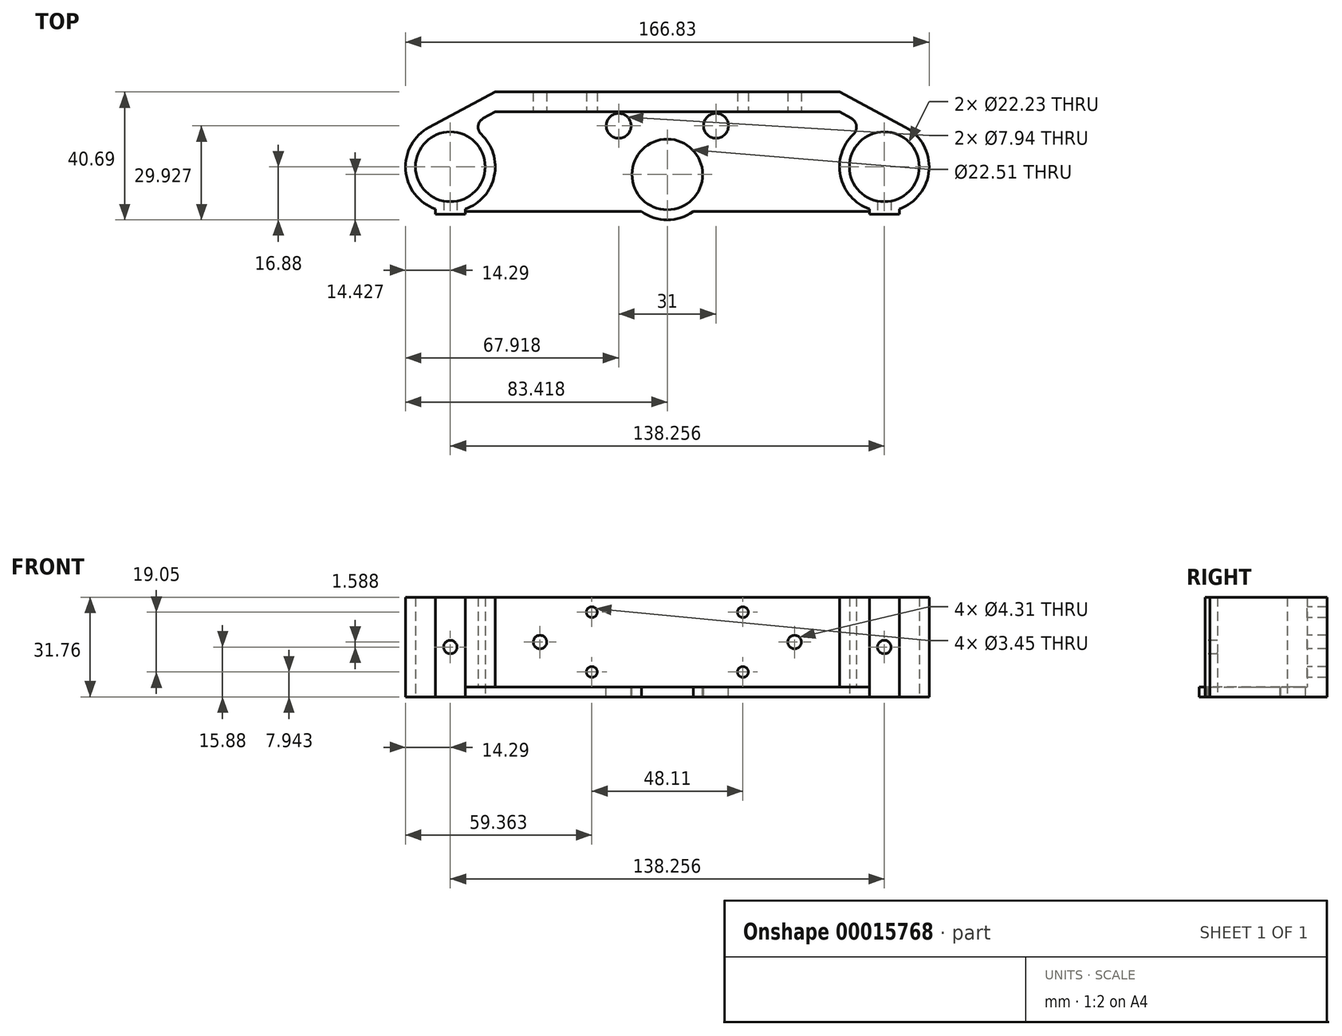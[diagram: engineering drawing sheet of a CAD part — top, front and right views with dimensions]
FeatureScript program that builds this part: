
annotation { "Feature Type Name" : "Feature", "Feature Type Description" : "" }
export const myFeature = defineFeature(function(context is Context, id is Id, definition is map)
    precondition{}
    {
        {
            var Q0;
            Q0=qCreatedBy(makeId("Top.planeOp"),FACE);
            var sketch = newSketch(context, id + "F0", { "sketchPlane" : qUnion([Q0])});
            skCircle(sketch, "E0", {"center": v(0, 0) * mm, "radius": 11.11 * mm});
            skLineSegment(sketch, "E1.bottom", {"start": v(14.29, 17.46) * mm, "end": v(123.97, 17.46) * mm});
            skLineSegment(sketch, "E2", {"start": v(69.13, 17.46) * mm, "end": v(69.13, 23.81) * mm, "construction": true});
            skCircle(sketch, "E3", {"center": v(138.26, 0) * mm, "radius": 11.11 * mm});
            skLineSegment(sketch, "E4", {"start": v(14.29, 23.81) * mm, "end": v(123.97, 23.81) * mm});
            skLineSegment(sketch, "E5", {"start": v(-6.72, 12.6) * mm, "end": v(14.29, 23.81) * mm});
            skLineSegment(sketch, "E6", {"start": v(123.97, 23.81) * mm, "end": v(144.98, 12.6) * mm});
            skLineSegment(sketch, "E7", {"start": v(0, 0) * mm, "end": v(138.26, 0) * mm, "construction": true});
            skLineSegment(sketch, "E8", {"start": v(69.13, 17.46) * mm, "end": v(69.13, 0) * mm, "construction": true});
            skLineSegment(sketch, "E9", {"start": v(123.97, 17.46) * mm, "end": v(132.33, 13) * mm});
            skLineSegment(sketch, "E10", {"start": v(128.15, 15.23) * mm, "end": v(130.79, 20.18) * mm, "construction": true});
            skLineSegment(sketch, "E11", {"start": v(5.92, 13) * mm, "end": v(14.29, 17.46) * mm});
            skArc(sketch, "E12", {"start": v(4.76, -13.47) * mm, "mid": v(14.27, -0.63) * mm, "end": v(5.92, 13) * mm});
            skArc(sketch, "E13", {"start": v(-6.72, 12.6) * mm, "mid": v(-14.25, -1.07) * mm, "end": v(-4.76, -13.47) * mm});
            skLineSegment(sketch, "E14", {"start": v(0, 0) * mm, "end": v(0, -13.47) * mm, "construction": true});
            skLineSegment(sketch, "E15", {"start": v(138.26, 0) * mm, "end": v(138.26, -13.47) * mm, "construction": true});
            skLineSegment(sketch, "E16.bottom", {"start": v(-4.76, -13.47) * mm, "end": v(4.76, -13.47) * mm, "construction": true});
            skLineSegment(sketch, "E16.top", {"start": v(-4.76, -15.06) * mm, "end": v(4.76, -15.06) * mm});
            skLineSegment(sketch, "E16.left", {"start": v(-4.76, -13.47) * mm, "end": v(-4.76, -15.06) * mm});
            skLineSegment(sketch, "E16.right", {"start": v(4.76, -13.47) * mm, "end": v(4.76, -15.06) * mm});
            skLineSegment(sketch, "E17.bottom", {"start": v(133.5, -13.47) * mm, "end": v(143.02, -13.47) * mm, "construction": true});
            skLineSegment(sketch, "E17.top", {"start": v(133.5, -15.06) * mm, "end": v(143.02, -15.06) * mm});
            skLineSegment(sketch, "E17.left", {"start": v(133.5, -13.47) * mm, "end": v(133.5, -15.06) * mm});
            skLineSegment(sketch, "E17.right", {"start": v(143.02, -13.47) * mm, "end": v(143.02, -15.06) * mm});
            skArc(sketch, "E18", {"start": v(132.33, 13) * mm, "mid": v(123.98, -0.63) * mm, "end": v(133.5, -13.47) * mm});
            skArc(sketch, "E19", {"start": v(143.02, -13.47) * mm, "mid": v(152.5, -1.07) * mm, "end": v(144.98, 12.6) * mm});
            skSolve(sketch);
        }
        {
            var Q0;
            Q0=qSketchRegion(id+"F0",true);
            extrude(context, id + "F1", {"entities" : qUnion([Q0]), "depth" : 28.57 * mm});
        }
        {
            var Q0;
            Q0=makeQuery(id+"F1.opExtrude","CAP_FACE",FACE,{"disambiguationData":[OSD([sQuery(id+"F0.wireOp",EDGE,"E0"),sQuery(id+"F0.wireOp",EDGE,"2iOkBpD2-QLiU-HpJU-IKXQ-EcRK06cCBt2a"),sQuery(id+"F0.wireOp",EDGE,"E1.bottom"),sQuery(id+"F0.wireOp",EDGE,"LR8YGM2p-kzYz-Rjs2-wGc3-v6aphVCy7C40"),sQuery(id+"F0.wireOp",EDGE,"E3"),sQuery(id+"F0.wireOp",EDGE,"E4"),sQuery(id+"F0.wireOp",EDGE,"E5"),sQuery(id+"F0.wireOp",EDGE,"E6"),sQuery(id+"F0.wireOp",EDGE,"E9"),sQuery(id+"F0.wireOp",EDGE,"E11")])],"isStart":true});
            var sketch = newSketch(context, id + "F2", { "sketchPlane" : qUnion([Q0])});
            skLineSegment(sketch, "E20", {"start": v(0, 0) * mm, "end": v(0, 14.29) * mm, "construction": true});
            skLineSegment(sketch, "E21", {"start": v(138.26, 14.29) * mm, "end": v(138.26, 0) * mm, "construction": true});
            skLineSegment(sketch, "E22", {"start": v(138.26, 0) * mm, "end": v(0, 0) * mm, "construction": true});
            skLineSegment(sketch, "E23", {"start": v(69.13, 0) * mm, "end": v(69.13, 2.45) * mm, "construction": true});
            skCircle(sketch, "E24", {"center": v(69.13, 2.45) * mm, "radius": 11.25 * mm});
            skLineSegment(sketch, "E25", {"start": v(138.26, 14.29) * mm, "end": v(77.38, 14.29) * mm});
            skLineSegment(sketch, "E26", {"start": v(0, 14.29) * mm, "end": v(60.87, 14.29) * mm});
            skArc(sketch, "E27", {"start": v(77.38, 14.29) * mm, "mid": v(69.13, 16.88) * mm, "end": v(60.87, 14.29) * mm});
            skLineSegment(sketch, "E28", {"start": v(69.13, 0) * mm, "end": v(69.13, -13.05) * mm, "construction": true});
            skLineSegment(sketch, "E29", {"start": v(84.63, -13.05) * mm, "end": v(53.63, -13.05) * mm, "construction": true});
            skCircle(sketch, "E30", {"center": v(84.63, -13.05) * mm, "radius": 3.97 * mm});
            skCircle(sketch, "E31", {"center": v(53.63, -13.05) * mm, "radius": 3.97 * mm});
            skSolve(sketch);
        }
        {
            var Q0;
            Q0=makeQuery(id+"F2.imprint","IMPRINT",FACE,{"disambiguationData":[TD([[makeQuery(id+"F2.imprint","IMPRINT",EDGE,{"derivedFrom":makeQuery(id+"F1.opExtrude","CAP_EDGE",EDGE,{"disambiguationData":[OSD([sQuery(id+"F0.wireOp",EDGE,"E0")])],"isStart":true})}),1.0]])]});
            var Q1;
            {var subQ2=sQuery(id+"F2.wireOp",EDGE,"SS8bNy7h-Ow7b-Kn8b-ZiMt-BjL3enOZ3Box");Q1=makeQuery(id+"F2.imprint","IMPRINT",FACE,{"disambiguationData":[TD([[makeQuery(id+"F2.imprint","IMPRINT",EDGE,{"derivedFrom":subQ2}),-1.0]])]});}
            var Q2;
            Q2=makeQuery(id+"F2.imprint","IMPRINT",FACE,{"disambiguationData":[TD([[makeQuery(id+"F2.imprint","IMPRINT",EDGE,{"derivedFrom":sQuery(id+"F2.wireOp",EDGE,"E24")}),-1.0]])]});
            extrude(context, id + "F3", {"entities" : qUnion([Q0, Q1, Q2]), "operationType" : NewBodyOperationType.ADD, "depth" : 3.17 * mm});
        }
        {
            var Q0;
            Q0=makeQuery(id+"F1.opExtrude","SWEPT_EDGE",EDGE,{"disambiguationData":[OSD([sQuery(id+"F0.wireOp",EDGE,"E11"),sQuery(id+"F0.wireOp",EDGE,"E12")])]});
            var Q1;
            Q1=makeQuery(id+"F1.opExtrude","SWEPT_EDGE",EDGE,{"disambiguationData":[OSD([sQuery(id+"F0.wireOp",EDGE,"E9"),sQuery(id+"F0.wireOp",EDGE,"E18")])]});
            fillet(context, id + "F4", {"entities" : qUnion([Q0, Q1]), "radius" : 3.17 * mm, "tangentPropagation" : true, "allowEdgeOverflow" : false});
        }
        {
            var Q0;
            Q0=makeQuery(id+"F1.opExtrude","SWEPT_FACE",FACE,{"disambiguationData":[OSD([sQuery(id+"F0.wireOp",EDGE,"E1.bottom")])]});
            var sketch = newSketch(context, id + "F5", { "sketchPlane" : qUnion([Q0])});
            skLineSegment(sketch, "E32", {"start": v(14.29, 14.29) * mm, "end": v(28.57, 14.29) * mm, "construction": true});
            skLineSegment(sketch, "E33", {"start": v(28.57, 14.29) * mm, "end": v(45.07, 14.29) * mm, "construction": true});
            skLineSegment(sketch, "E34", {"start": v(45.07, 14.29) * mm, "end": v(93.18, 14.29) * mm, "construction": true});
            skLineSegment(sketch, "E35", {"start": v(93.18, 14.29) * mm, "end": v(109.68, 14.29) * mm, "construction": true});
            skLineSegment(sketch, "E36", {"start": v(109.68, 14.29) * mm, "end": v(123.97, 14.29) * mm, "construction": true});
            skLineSegment(sketch, "E37", {"start": v(45.07, 23.81) * mm, "end": v(45.07, 4.76) * mm, "construction": true});
            skLineSegment(sketch, "E38", {"start": v(93.18, 23.81) * mm, "end": v(93.18, 4.76) * mm, "construction": true});
            skLineSegment(sketch, "E39", {"start": v(93.18, 23.81) * mm, "end": v(93.18, 28.58) * mm, "construction": true});
            skCircle(sketch, "E40", {"center": v(28.57, 14.29) * mm, "radius": 2.15 * mm});
            skCircle(sketch, "E41", {"center": v(109.68, 14.29) * mm, "radius": 2.15 * mm});
            skCircle(sketch, "E42", {"center": v(93.18, 4.76) * mm, "radius": 1.73 * mm});
            skCircle(sketch, "E43", {"center": v(93.18, 23.81) * mm, "radius": 1.73 * mm});
            skCircle(sketch, "E44", {"center": v(45.07, 23.81) * mm, "radius": 1.73 * mm});
            skCircle(sketch, "E45", {"center": v(45.07, 4.76) * mm, "radius": 1.73 * mm});
            skSolve(sketch);
        }
        {
            var Q0;
            Q0 = qSketchRegion(id + "F5", true);
            var Q1;
            {var subQ0=sQuery(id+"F0.wireOp",EDGE,"E4");Q1=makeQuery(id+"F3.boolean.opBoolean","MERGE",FACE,{"derivedFrom":[makeQuery(id+"F1.opExtrude","SWEPT_FACE",FACE,{"disambiguationData":[OSD([subQ0])]}),makeQuery(id+"F3.opExtrude","SWEPT_FACE",FACE,{"disambiguationData":[OSD([subQ0])]})]});}
            extrude(context, id + "F6", {"entities" : qUnion([Q0]), "operationType" : NewBodyOperationType.REMOVE, "endBound" : BoundingType.UP_TO_SURFACE, "oppositeDirection" : true, "endBoundEntityFace" : qUnion([Q1]), "depth" : 25.4 * mm});
        }
        {
            var Q0;
            {var subQ0=sQuery(id+"F0.wireOp",EDGE,"E17.top");Q0=makeQuery(id+"F3.boolean.opBoolean","MERGE",FACE,{"derivedFrom":[makeQuery(id+"F1.opExtrude","SWEPT_FACE",FACE,{"disambiguationData":[OSD([sQuery(id+"F0.wireOp",EDGE,"E16.top")])]}),makeQuery(id+"F1.opExtrude","SWEPT_FACE",FACE,{"disambiguationData":[OSD([subQ0])]}),makeQuery(id+"F3.opExtrude","SWEPT_FACE",FACE,{"disambiguationData":[OSD([subQ0,sQuery(id+"F2.wireOp",EDGE,"SS8bNy7h-Ow7b-Kn8b-ZiMt-BjL3enOZ3Box")])]})]});}
            var sketch = newSketch(context, id + "F7", { "sketchPlane" : qUnion([Q0])});
            skLineSegment(sketch, "E46", {"start": v(0, 28.58) * mm, "end": v(0, -3.18) * mm, "construction": true});
            skLineSegment(sketch, "E47", {"start": v(138.26, 28.58) * mm, "end": v(138.26, -3.18) * mm, "construction": true});
            skCircle(sketch, "E48", {"center": v(0, 12.7) * mm, "radius": 2.15 * mm});
            skCircle(sketch, "E49", {"center": v(138.26, 12.7) * mm, "radius": 2.15 * mm});
            skSolve(sketch);
        }
        {
            var Q0;
            Q0 = qSketchRegion(id + "F7", true);
            var Q1;
            {var subQ0=sQuery(id+"F0.wireOp",EDGE,"E0");Q1=makeQuery(id+"F3.boolean.opBoolean","MERGE",FACE,{"derivedFrom":[makeQuery(id+"F1.opExtrude","SWEPT_FACE",FACE,{"disambiguationData":[OSD([subQ0])]}),makeQuery(id+"F3.opExtrude","SWEPT_FACE",FACE,{"disambiguationData":[OSD([subQ0])]})]});}
            extrude(context, id + "F8", {"entities" : qUnion([Q0]), "operationType" : NewBodyOperationType.REMOVE, "oppositeDirection" : true, "endBoundEntityFace" : qUnion([Q1]), "depth" : 6.35 * mm});
        }
    });
